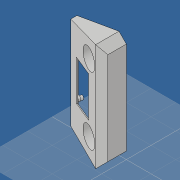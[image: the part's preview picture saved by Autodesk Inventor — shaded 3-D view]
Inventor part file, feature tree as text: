
AUTODESK INVENTOR PART (.ipt)
format: ipt  version: 2019 (Build 230136000, 136)  size: 264,192 bytes
history: native  units: mm
features: extrude x10, sketch x4, shell x1, hole x1, fillet x1, projected_geometry x1
ambient origin geometry x8: Origin, YZ Plane, XZ Plane, XY Plane, X Axis, Y Axis, Z Axis, Center Point
bodies: Volumenkörper1 (feature_tree)
feature tree (18):
  sketch  "Skizze2"  dims[d0=40.0mm d2=75.0mm d3=0.0mm d4=1.2mm]
  extrude  "Extrusion1"  Depth=1.2mm TaperAngle=0.0deg
  shell  "Wandung1"  Thickness=1.2mm
  sketch  "Skizze3"  dims[d12=35.75mm d13=3.0mm d16=75.0mm d17=0.0mm d20=2.0mm d21=0.0mm]
  extrude  "Extrusion2"  Depth=2.0mm TaperAngle=0.0deg
  extrude  "Extrusion4"  Depth=2.0mm TaperAngle=0.0deg
  extrude  "Extrusion11"  Depth=1.0mm
  extrude  "Extrusion15"  Depth=5.0mm
  sketch  "Skizze5"  dims[d30=16.0mm d34=2.0mm d35=0.0mm]
  extrude  "Extrusion7"  Depth=15.0mm
  extrude  "Extrusion8"  Depth=6.0mm
  extrude  "Extrusion10"  Depth=1.0mm
  hole  "Bohrung1"  [1 undecoded]
  sketch  "Skizze6"  dims[d36=2.0mm d37=0.0mm d38=1.0mm d40=5.0mm d43=15.0mm d45=6.0mm d46=21.816616mm d47=7.0mm d48=5.0mm d49=2.2mm d50=6.0mm d51=4.0mm d52=2.0mm d53=90.0deg d54=6.0mm d55=0.0mm d56=5.0mm d59=2.0mm d60=0.0mm d63=2.5mm d65=0.0mm d66=33.5mm d67=23.5mm d68=34.5mm d69=31.0mm d70=28.5mm d71=2.5mm d72=2.5mm d73=5.0mm d74=3.75mm d75=4.0mm d76=0.0mm d77=14.0mm d80=6.0mm d81=21.816616mm d82=0.0mm d83=1.0mm d84=0.0mm d87=1.0mm d88=0.0mm d90=0.5mm d91=0.5mm d92=0.0mm d93=5.0mm d94=1.0mm d95=1.0mm]
  extrude  "Extrusion12"  Depth=5.0mm
  extrude  "Extrusion14"  Depth=5.0mm
  fillet  "Rundung1"  Radius=2.0mm
  projected_geometry  "Projizierte Kontur1"
note: 1 required parameter value undecoded (feature->parameter linkage not recoverable at this tier; creation-order binding heuristic only, values carry confidence <= 0.55)
